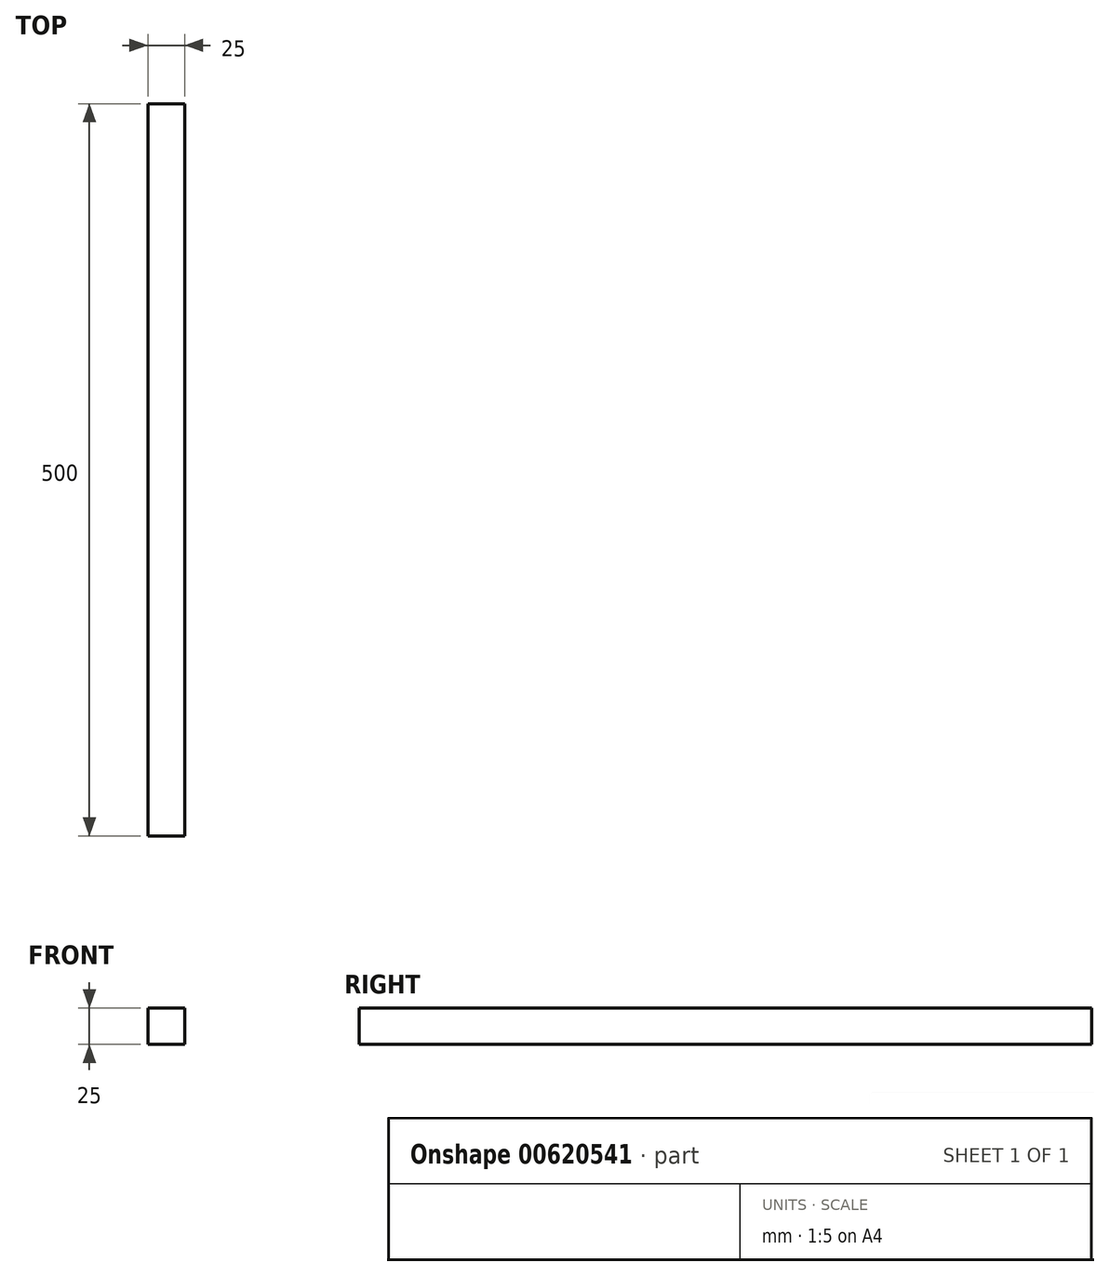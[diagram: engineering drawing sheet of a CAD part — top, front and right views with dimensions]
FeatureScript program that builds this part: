
annotation { "Feature Type Name" : "Feature", "Feature Type Description" : "" }
export const myFeature = defineFeature(function(context is Context, id is Id, definition is map)
    precondition{}
    {
        {
            var Q0;
            Q0=qCreatedBy(makeId("Front.planeOp"),FACE);
            var sketch = newSketch(context, id + "F0", { "sketchPlane" : qUnion([Q0])});
            skLineSegment(sketch, "E0.bottom", {"start": v(12.5, 12.5) * mm, "end": v(-12.5, 12.5) * mm});
            skLineSegment(sketch, "E0.top", {"start": v(12.5, -12.5) * mm, "end": v(-12.5, -12.5) * mm});
            skLineSegment(sketch, "E0.left", {"start": v(12.5, 12.5) * mm, "end": v(12.5, -12.5) * mm});
            skLineSegment(sketch, "E0.right", {"start": v(-12.5, 12.5) * mm, "end": v(-12.5, -12.5) * mm});
            skPoint(sketch, "E0.middle", {"position": v(0, 0) * mm});
            skSolve(sketch);
        }
        {
            var Q0;
            Q0 = qSketchRegion(id + "F0", true);
            extrude(context, id + "F1", {"entities" : qUnion([Q0]), "depth" : 500 * mm, "offsetDistance" : 25 * mm});
        }
    });
